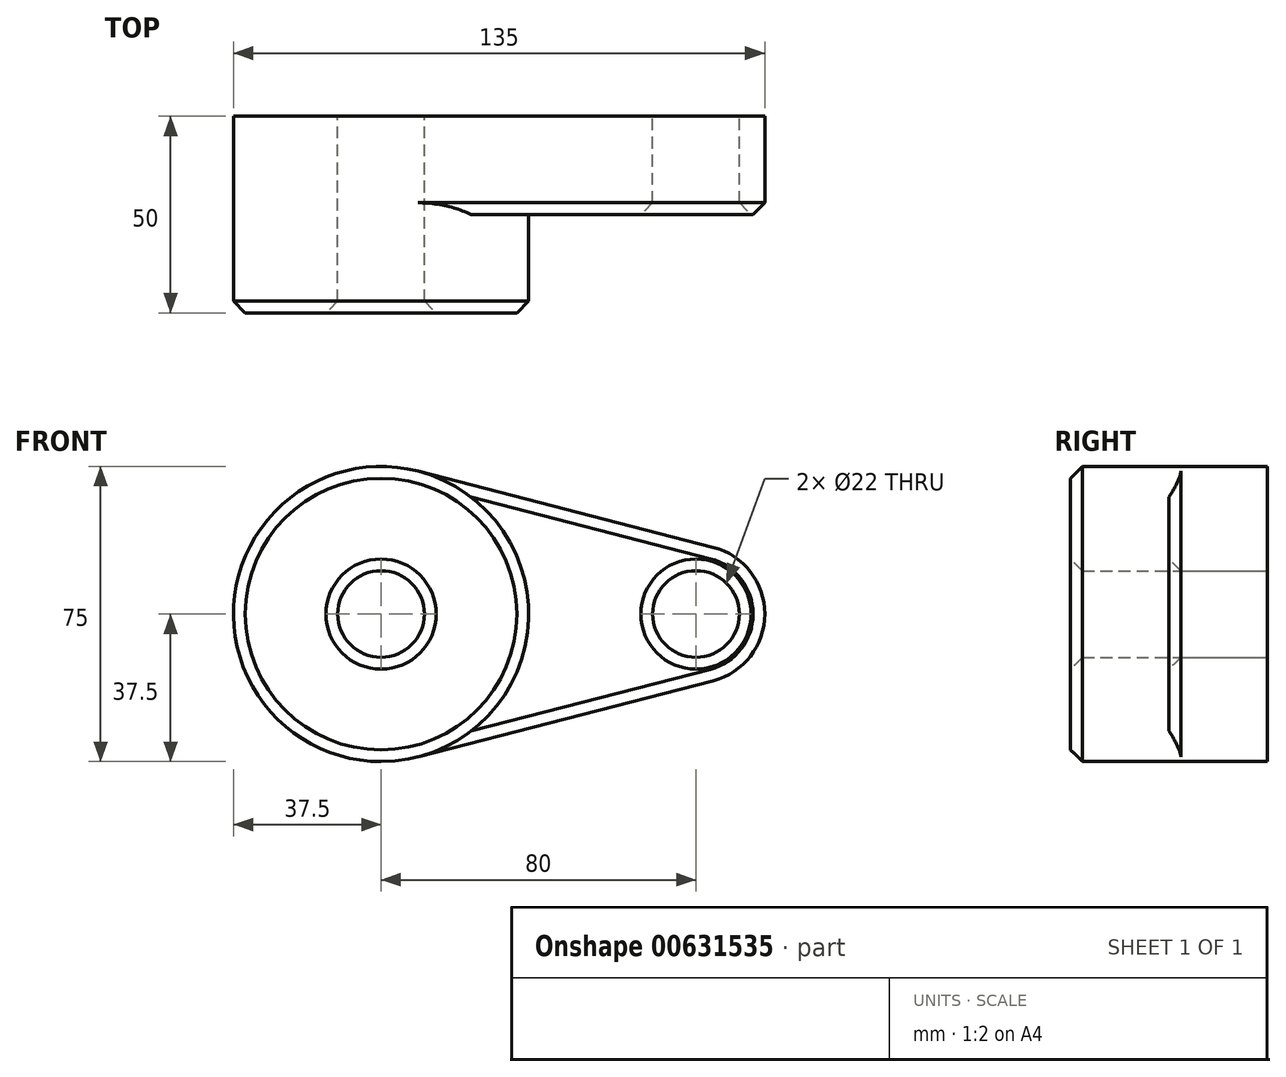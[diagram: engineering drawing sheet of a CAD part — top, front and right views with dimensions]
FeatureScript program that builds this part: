
annotation { "Feature Type Name" : "Feature", "Feature Type Description" : "" }
export const myFeature = defineFeature(function(context is Context, id is Id, definition is map)
    precondition{}
    {
        {
            var Q0;
            Q0=qCreatedBy(makeId("Front.planeOp"),FACE);
            var sketch = newSketch(context, id + "F0", { "sketchPlane" : qUnion([Q0])});
            skCircle(sketch, "E0", {"center": v(0, 0) * mm, "radius": 37.5 * mm});
            skCircle(sketch, "E1", {"center": v(80, 0) * mm, "radius": 17.5 * mm});
            skLineSegment(sketch, "E2", {"start": v(9.37, 36.3) * mm, "end": v(84.38, 16.94) * mm});
            skLineSegment(sketch, "E3", {"start": v(9.37, -36.3) * mm, "end": v(84.38, -16.94) * mm});
            skCircle(sketch, "E4", {"center": v(0, 0) * mm, "radius": 11 * mm});
            skCircle(sketch, "E5", {"center": v(80, 0) * mm, "radius": 11 * mm});
            skSolve(sketch);
        }
        {
            var Q0;
            Q0 = qSketchRegion(id + "F0", true);
            extrude(context, id + "F1", {"entities" : qUnion([Q0]), "depth" : 25 * mm, "offsetDistance" : 25 * mm});
        }
        {
            var Q0;
            Q0=makeQuery(id+"F0.imprint","IMPRINT",FACE,{"disambiguationData":[TD([[makeQuery(id+"F0.imprint","IMPRINT",EDGE,{"derivedFrom":sQuery(id+"F0.wireOp",EDGE,"E4")}),-1.0]])]});
            extrude(context, id + "F2", {"entities" : qUnion([Q0]), "operationType" : NewBodyOperationType.ADD, "depth" : 50 * mm, "offsetDistance" : 25 * mm});
        }
        {
            var Q0;
            Q0=makeQuery(id+"F1.opExtrude","CAP_EDGE",EDGE,{"disambiguationData":[OSD([sQuery(id+"F0.wireOp",EDGE,"E2")])],"isStart":false});
            var Q1;
            Q1=makeQuery(id+"F1.opExtrude","CAP_EDGE",EDGE,{"disambiguationData":[OSD([sQuery(id+"F0.wireOp",EDGE,"E1")])],"isStart":false});
            var Q2;
            Q2=makeQuery(id+"F1.opExtrude","CAP_EDGE",EDGE,{"disambiguationData":[OSD([sQuery(id+"F0.wireOp",EDGE,"E5")])],"isStart":false});
            var Q3;
            Q3=makeQuery(id+"F2.opExtrude","CAP_EDGE",EDGE,{"disambiguationData":[OSD([sQuery(id+"F0.wireOp",EDGE,"E4")])],"isStart":false});
            var Q4;
            Q4=makeQuery(id+"F2.opExtrude","CAP_EDGE",EDGE,{"disambiguationData":[OSD([sQuery(id+"F0.wireOp",EDGE,"E0")])],"isStart":false});
            chamfer(context, id + "F3", {"entities" : qUnion([Q0, Q1, Q2, Q3, Q4]), "width" : 3 * mm, "tangentPropagation" : true});
        }
    });
